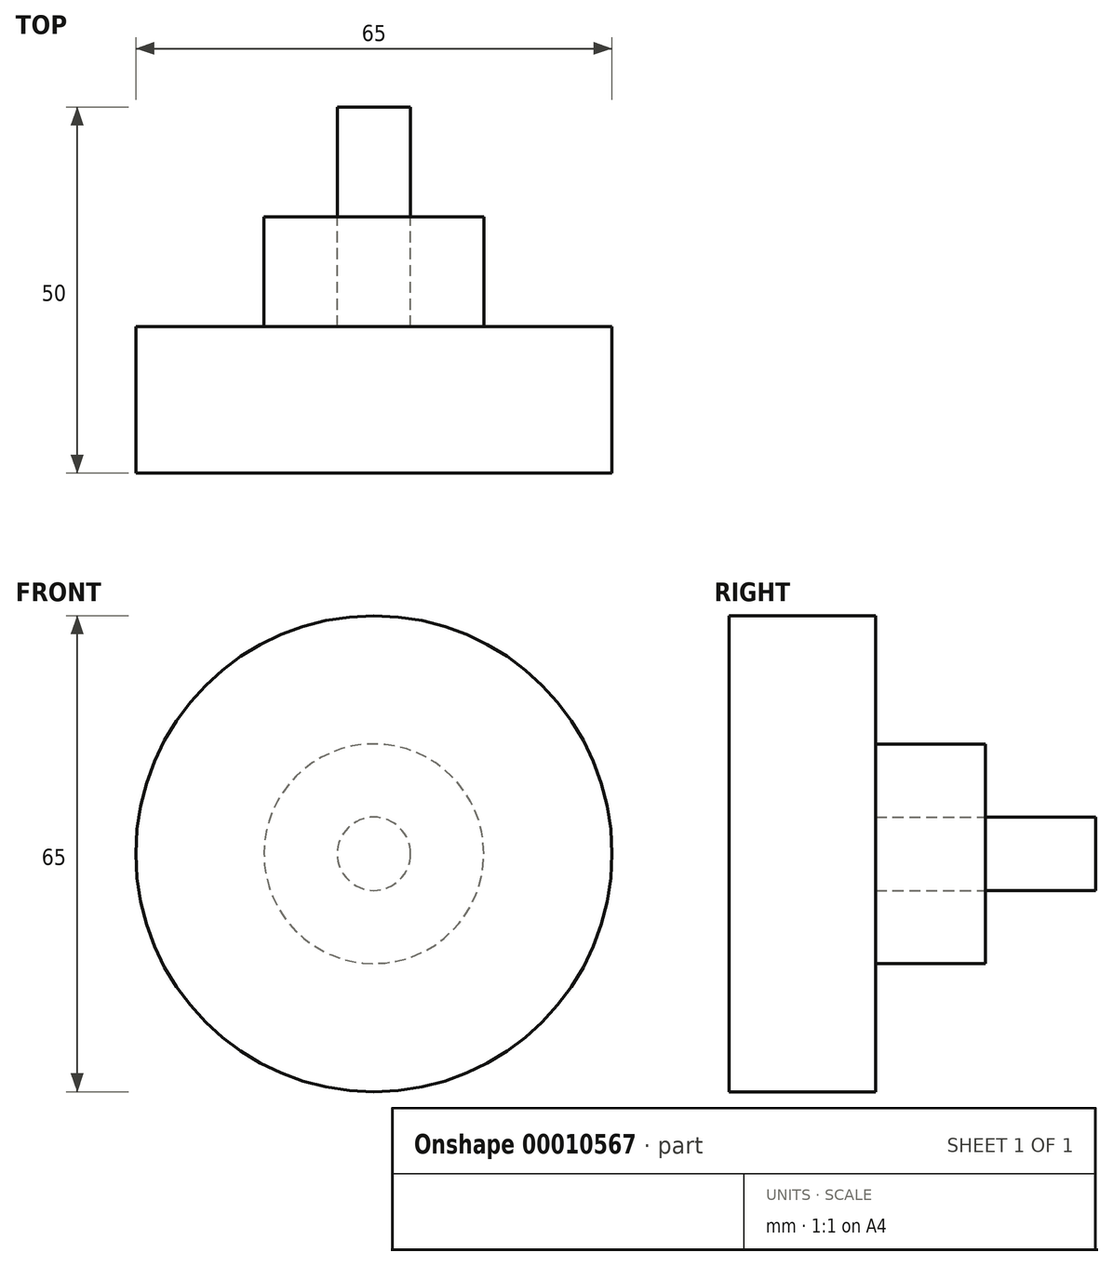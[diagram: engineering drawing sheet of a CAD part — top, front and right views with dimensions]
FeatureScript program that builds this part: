
annotation { "Feature Type Name" : "Feature", "Feature Type Description" : "" }
export const myFeature = defineFeature(function(context is Context, id is Id, definition is map)
    precondition{}
    {
        {
            var Q0;
            Q0=qCreatedBy(makeId("Right.planeOp"),FACE);
            var sketch = newSketch(context, id + "F0", { "sketchPlane" : qUnion([Q0])});
            skLineSegment(sketch, "E0.rect.bottom", {"start": v(0, 5) * mm, "end": v(-30, 5) * mm});
            skLineSegment(sketch, "E0.rect.top", {"start": v(0, -5) * mm, "end": v(-30, -5) * mm});
            skLineSegment(sketch, "E0.rect.left", {"start": v(0, 5) * mm, "end": v(0, -5) * mm});
            skLineSegment(sketch, "E0.rect.right", {"start": v(-30, 5) * mm, "end": v(-30, -5) * mm});
            skPoint(sketch, "E0.rect.middle", {"position": v(-15, 0) * mm});
            skLineSegment(sketch, "E1.rect.bottom", {"start": v(-50, 32.5) * mm, "end": v(-30, 32.5) * mm});
            skLineSegment(sketch, "E1.rect.top", {"start": v(-50, -32.5) * mm, "end": v(-30, -32.5) * mm});
            skLineSegment(sketch, "E1.rect.left", {"start": v(-50, 32.5) * mm, "end": v(-50, -32.5) * mm});
            skLineSegment(sketch, "E1.rect.right", {"start": v(-30, 32.5) * mm, "end": v(-30, -32.5) * mm});
            skPoint(sketch, "E1.rect.middle", {"position": v(-40, 0) * mm});
            skLineSegment(sketch, "E2", {"start": v(0, 0) * mm, "end": v(-50, 0) * mm});
            skLineSegment(sketch, "E3.bottom", {"start": v(-30, 15) * mm, "end": v(-15, 15) * mm});
            skLineSegment(sketch, "E3.top", {"start": v(-30, -15) * mm, "end": v(-15, -15) * mm});
            skLineSegment(sketch, "E3.left", {"start": v(-30, 15) * mm, "end": v(-30, -15) * mm});
            skLineSegment(sketch, "E3.right", {"start": v(-15, 15) * mm, "end": v(-15, -15) * mm});
            skSolve(sketch);
        }
        {
            var Q0;
            {var subQ8=sQuery(id+"F0.wireOp",EDGE,"E1.rect.bottom");Q0=makeQuery(id+"F0.imprint","IMPRINT",FACE,{"disambiguationData":[TD([[makeQuery(id+"F0.imprint","IMPRINT",EDGE,{"derivedFrom":subQ8}),-1.0]])]});}
            var Q1;
            {var subQ3=sQuery(id+"F0.wireOp",EDGE,"E3.bottom");Q1=makeQuery(id+"F0.imprint","IMPRINT",FACE,{"disambiguationData":[TD([[makeQuery(id+"F0.imprint","IMPRINT",EDGE,{"derivedFrom":subQ3}),-1.0]])]});}
            var Q2;
            {var subQ3=sQuery(id+"F0.wireOp",EDGE,"E0.rect.bottom");var subQ5=sQuery(id+"F0.wireOp",EDGE,"E3.left");var subQ7=makeQuery(id+"F0.imprint","INTERSECT",VERTEX,{"derivedFrom":[subQ3,subQ5]});Q2=makeQuery(id+"F0.imprint","IMPRINT",FACE,{"disambiguationData":[TD([[makeQuery(id+"F0.imprint","IMPRINT",EDGE,{"disambiguationData":[TD([[subQ7,1.0]])],"derivedFrom":subQ3}),1.0]])]});}
            var Q3;
            {var subQ3=sQuery(id+"F0.wireOp",EDGE,"E0.rect.bottom");var subQ5=sQuery(id+"F0.wireOp",EDGE,"E0.rect.left");var subQ7=makeQuery(id+"F0.imprint","INTERSECT",VERTEX,{"derivedFrom":[subQ3,subQ5]});Q3=makeQuery(id+"F0.imprint","IMPRINT",FACE,{"disambiguationData":[TD([[makeQuery(id+"F0.imprint","IMPRINT",EDGE,{"disambiguationData":[TD([[subQ7,-1.0]])],"derivedFrom":subQ3}),1.0]])]});}
            var Q4;
            Q4=sQuery(id+"F0.wireOp",EDGE,"E2");
            revolve(context, id + "F1", {"entities" : qUnion([Q0, Q1, Q2, Q3]), "axis" : qUnion([Q4]), "revolveType" : RevolveType.FULL});
        }
    });
